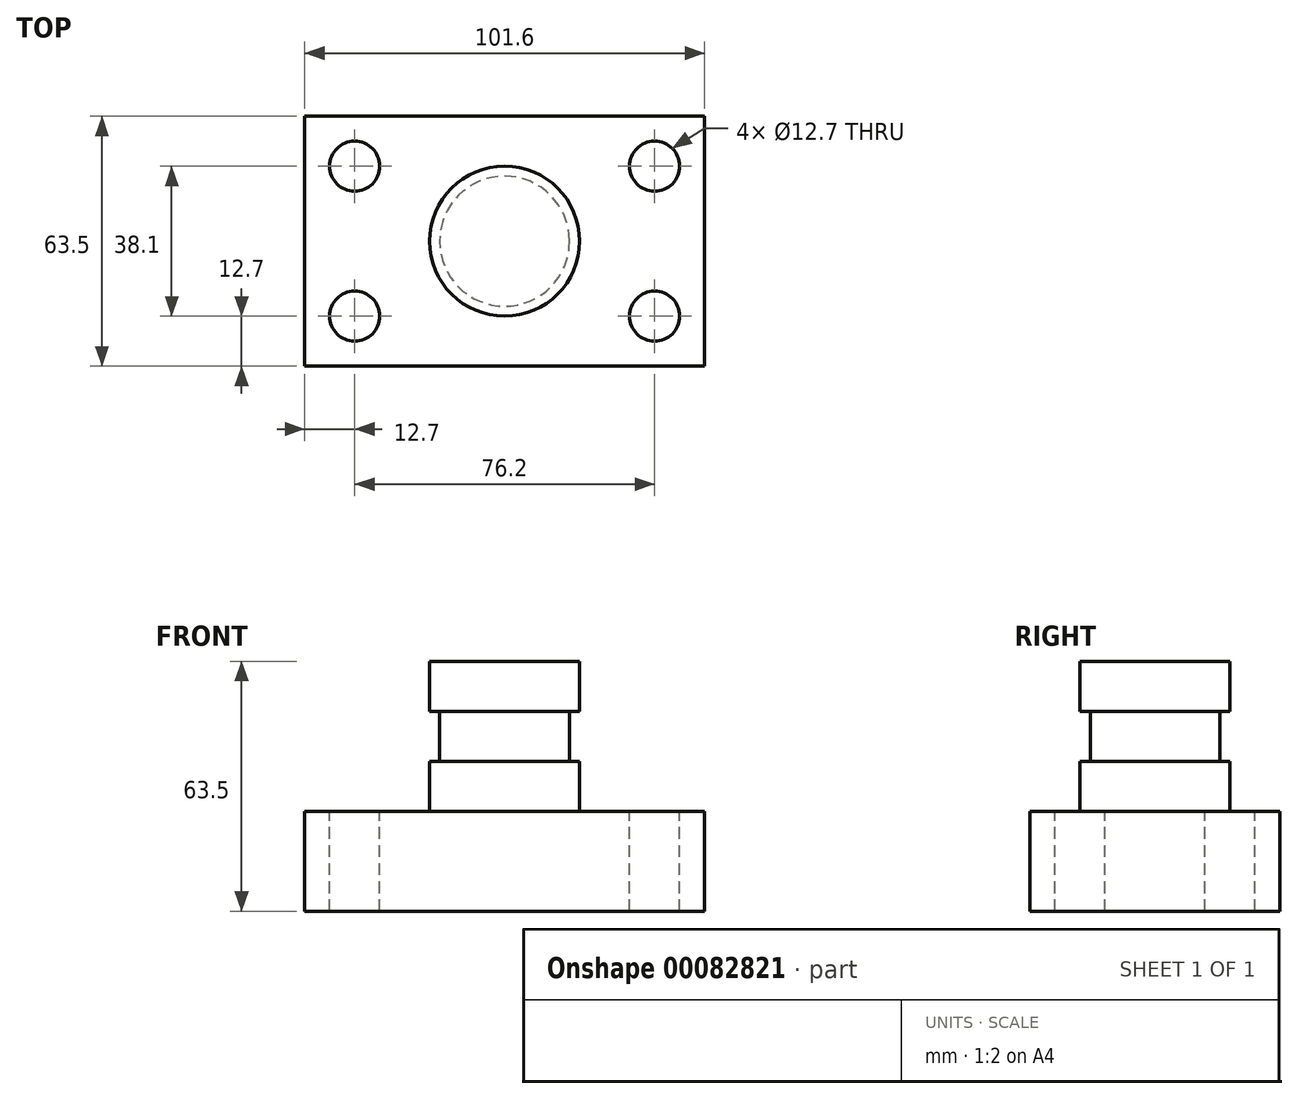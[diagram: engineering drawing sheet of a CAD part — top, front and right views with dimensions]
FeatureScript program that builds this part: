
annotation { "Feature Type Name" : "Feature", "Feature Type Description" : "" }
export const myFeature = defineFeature(function(context is Context, id is Id, definition is map)
    precondition{}
    {
        {
            var Q0;
            Q0=qCreatedBy(makeId("Top.planeOp"),FACE);
            var sketch = newSketch(context, id + "F0", { "sketchPlane" : qUnion([Q0])});
            skLineSegment(sketch, "E0", {"start": v(-50.8, 31.75) * mm, "end": v(50.8, 31.75) * mm});
            skLineSegment(sketch, "E1", {"start": v(50.8, 31.75) * mm, "end": v(50.8, -31.75) * mm});
            skLineSegment(sketch, "E2", {"start": v(50.8, -31.75) * mm, "end": v(-50.8, -31.75) * mm});
            skLineSegment(sketch, "E3", {"start": v(-50.8, -31.75) * mm, "end": v(-50.8, 31.75) * mm});
            skSolve(sketch);
        }
        {
            var Q0;
            Q0 = qSketchRegion(id + "F0", true);
            extrude(context, id + "F1", {"entities" : qUnion([Q0]), "depth" : 25.4 * mm});
        }
        {
            var Q0;
            Q0=makeQuery(id+"F1.opExtrude","CAP_FACE",FACE,{"disambiguationData":[OSD([sQuery(id+"F0.wireOp",EDGE,"E0"),sQuery(id+"F0.wireOp",EDGE,"E1"),sQuery(id+"F0.wireOp",EDGE,"E2"),sQuery(id+"F0.wireOp",EDGE,"E3")])],"isStart":false});
            var sketch = newSketch(context, id + "F2", { "sketchPlane" : qUnion([Q0])});
            skCircle(sketch, "E4", {"center": v(-38.1, 19.05) * mm, "radius": 6.35 * mm});
            skCircle(sketch, "E5", {"center": v(-38.1, -19.05) * mm, "radius": 6.35 * mm});
            skCircle(sketch, "E6.MirrorC", {"center": v(38.1, 19.05) * mm, "radius": 6.35 * mm});
            skCircle(sketch, "E7.MirrorC", {"center": v(38.1, -19.05) * mm, "radius": 6.35 * mm});
            skSolve(sketch);
        }
        {
            var Q0;
            Q0 = qSketchRegion(id + "F2", true);
            extrude(context, id + "F3", {"entities" : qUnion([Q0]), "operationType" : NewBodyOperationType.REMOVE, "endBound" : BoundingType.THROUGH_ALL, "oppositeDirection" : true, "depth" : 25.4 * mm});
        }
        {
            var Q0;
            Q0=qCreatedBy(makeId("Front.planeOp"),FACE);
            var sketch = newSketch(context, id + "F4", { "sketchPlane" : qUnion([Q0])});
            skLineSegment(sketch, "E8.bottom", {"start": v(0, 63.5) * mm, "end": v(-19.05, 63.5) * mm});
            skLineSegment(sketch, "E8.top", {"start": v(0, 25.4) * mm, "end": v(-19.05, 25.4) * mm});
            skLineSegment(sketch, "E8.left", {"start": v(0, 63.5) * mm, "end": v(0, 25.4) * mm});
            skLineSegment(sketch, "E8.right", {"start": v(-19.05, 63.5) * mm, "end": v(-19.05, 25.4) * mm});
            skSolve(sketch);
        }
        {
            var Q0;
            Q0=makeQuery(id+"F4.imprint","IMPRINT",FACE,{"disambiguationData":[TD([[makeQuery(id+"F4.imprint","IMPRINT",EDGE,{"derivedFrom":sQuery(id+"F4.wireOp",EDGE,"E8.bottom")}),1.0]])]});
            var Q1;
            Q1=sQuery(id+"F4.wireOp",EDGE,"E8.left");
            revolve(context, id + "F5", {"operationType" : NewBodyOperationType.ADD, "entities" : qUnion([Q0]), "axis" : qUnion([Q1]), "revolveType" : RevolveType.FULL, "oppositeDirection" : true});
        }
        {
            var Q0;
            Q0=qCreatedBy(makeId("Front.planeOp"),FACE);
            var sketch = newSketch(context, id + "F6", { "sketchPlane" : qUnion([Q0])});
            skLineSegment(sketch, "E9", {"start": v(-19.05, 38.1) * mm, "end": v(-19.05, 50.8) * mm});
            skLineSegment(sketch, "E10", {"start": v(-19.05, 50.8) * mm, "end": v(-16.5, 50.8) * mm});
            skLineSegment(sketch, "E11", {"start": v(-16.5, 50.8) * mm, "end": v(-16.5, 38.1) * mm});
            skLineSegment(sketch, "E12", {"start": v(-16.5, 38.1) * mm, "end": v(-19.05, 38.1) * mm});
            skSolve(sketch);
        }
        {
            var Q0;
            Q0=qCreatedBy(makeId("Front.planeOp"),FACE);
            var sketch = newSketch(context, id + "F7", { "sketchPlane" : qUnion([Q0])});
            skLineSegment(sketch, "E13", {"start": v(0, 67.87) * mm, "end": v(0, 20.72) * mm, "construction": true});
            skSolve(sketch);
        }
        {
            var Q0;
            Q0 = qSketchRegion(id + "F6", true);
            var Q1;
            Q1=sQuery(id+"F7.wireOp",EDGE,"E13");
            revolve(context, id + "F8", {"operationType" : NewBodyOperationType.REMOVE, "entities" : qUnion([Q0]), "axis" : qUnion([Q1]), "revolveType" : RevolveType.FULL, "oppositeDirection" : true});
        }
    });
